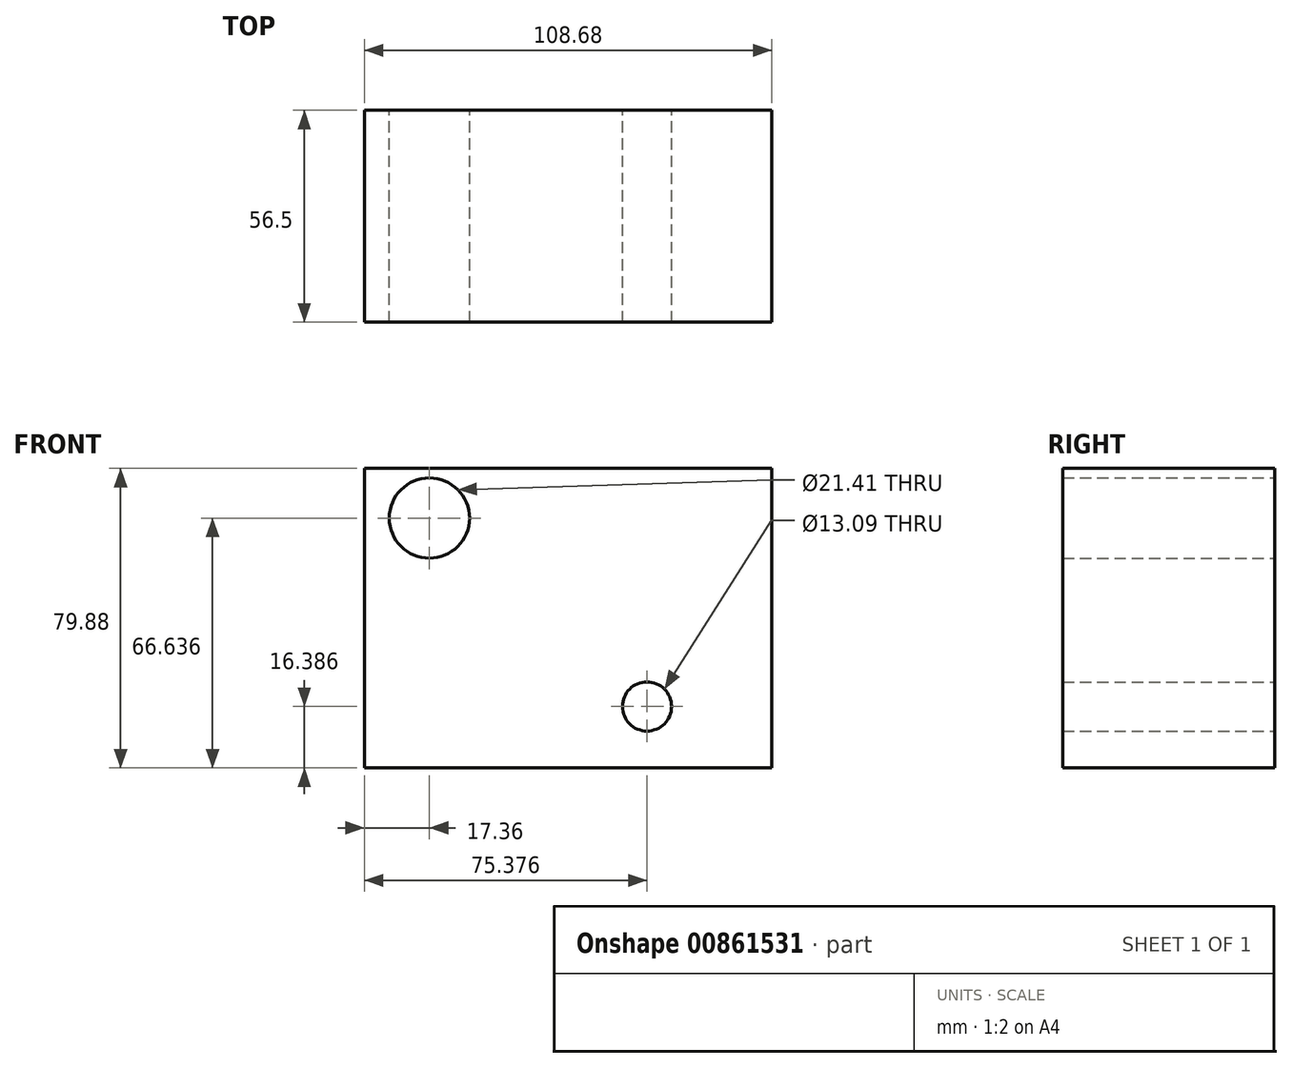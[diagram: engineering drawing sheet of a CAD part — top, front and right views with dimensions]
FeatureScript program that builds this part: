
annotation { "Feature Type Name" : "Feature", "Feature Type Description" : "" }
export const myFeature = defineFeature(function(context is Context, id is Id, definition is map)
    precondition{}
    {
        {
            var Q0;
            Q0=qCreatedBy(makeId("Front.planeOp"),FACE);
            var sketch = newSketch(context, id + "F0", { "sketchPlane" : qUnion([Q0])});
            skLineSegment(sketch, "E0.bottom", {"start": v(-54.34, 39.94) * mm, "end": v(54.34, 39.94) * mm});
            skLineSegment(sketch, "E0.top", {"start": v(-54.34, -39.94) * mm, "end": v(54.34, -39.94) * mm});
            skLineSegment(sketch, "E0.left", {"start": v(-54.34, 39.94) * mm, "end": v(-54.34, -39.94) * mm});
            skLineSegment(sketch, "E0.right", {"start": v(54.34, 39.94) * mm, "end": v(54.34, -39.94) * mm});
            skPoint(sketch, "E0.middle", {"position": v(0, 0) * mm});
            skCircle(sketch, "E1", {"center": v(-36.98, 26.7) * mm, "radius": 10.7 * mm});
            skCircle(sketch, "E2", {"center": v(21.04, -23.55) * mm, "radius": 6.54 * mm});
            skSolve(sketch);
        }
        {
            var Q0;
            Q0=makeQuery(id+"F0.imprint","IMPRINT",FACE,{"disambiguationData":[TD([[makeQuery(id+"F0.imprint","IMPRINT",EDGE,{"derivedFrom":sQuery(id+"F0.wireOp",EDGE,"E0.bottom")}),-1.0]])]});
            extrude(context, id + "F1", {"entities" : qUnion([Q0]), "depth" : 56.5 * mm, "offsetDistance" : 25 * mm});
        }
    });
